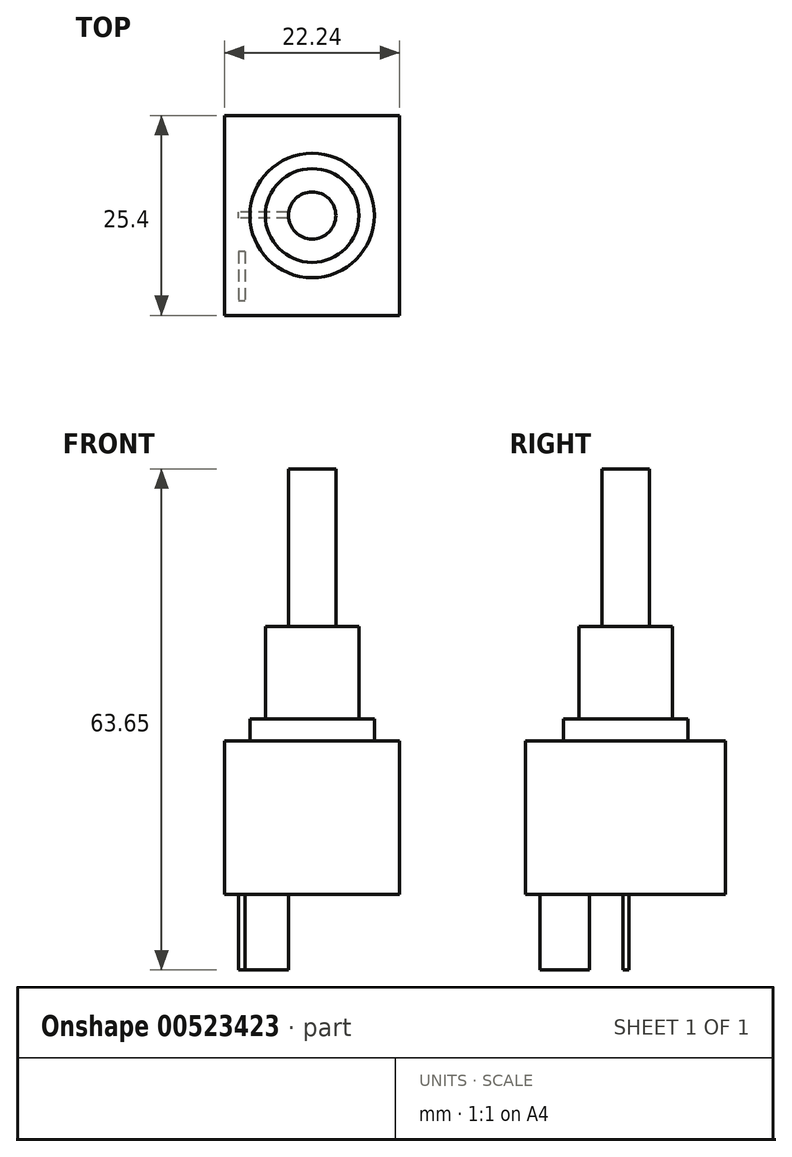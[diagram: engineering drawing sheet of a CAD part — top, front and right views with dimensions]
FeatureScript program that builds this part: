
annotation { "Feature Type Name" : "Feature", "Feature Type Description" : "" }
export const myFeature = defineFeature(function(context is Context, id is Id, definition is map)
    precondition{}
    {
        {
            var Q0;
            Q0=qCreatedBy(makeId("Top.planeOp"),FACE);
            var sketch = newSketch(context, id + "F0", { "sketchPlane" : qUnion([Q0])});
            skLineSegment(sketch, "E0.bottom", {"start": v(11.13, 12.7) * mm, "end": v(-11.12, 12.7) * mm});
            skLineSegment(sketch, "E0.top", {"start": v(11.12, -12.7) * mm, "end": v(-11.13, -12.7) * mm});
            skLineSegment(sketch, "E0.left", {"start": v(11.13, 12.7) * mm, "end": v(11.12, -12.7) * mm});
            skLineSegment(sketch, "E0.right", {"start": v(-11.13, 12.7) * mm, "end": v(-11.13, -12.7) * mm});
            skPoint(sketch, "E0.middle", {"position": v(0, 0) * mm});
            skSolve(sketch);
        }
        {
            var Q0;
            Q0 = qSketchRegion(id + "F0", true);
            extrude(context, id + "F1", {"entities" : qUnion([Q0]), "depth" : 19.5 * mm, "offsetDistance" : 25 * mm});
        }
        {
            var Q0;
            Q0=makeQuery(id+"F1.opExtrude","CAP_FACE",FACE,{"disambiguationData":[OSD([sQuery(id+"F0.wireOp",EDGE,"E0.bottom"),sQuery(id+"F0.wireOp",EDGE,"E0.top"),sQuery(id+"F0.wireOp",EDGE,"E0.left"),sQuery(id+"F0.wireOp",EDGE,"E0.right")])],"isStart":false});
            var sketch = newSketch(context, id + "F2", { "sketchPlane" : qUnion([Q0])});
            skCircle(sketch, "E1", {"center": v(0, 0) * mm, "radius": 7.9 * mm});
            skCircle(sketch, "E2", {"center": v(0, 0) * mm, "radius": 5.95 * mm});
            skSolve(sketch);
        }
        {
            var Q0;
            Q0=makeQuery(id+"F2.imprint","IMPRINT",FACE,{"disambiguationData":[TD([[makeQuery(id+"F2.imprint","IMPRINT",EDGE,{"derivedFrom":sQuery(id+"F2.wireOp",EDGE,"E2")}),1.0]])]});
            var Q1;
            Q1=makeQuery(id+"F2.imprint","IMPRINT",FACE,{"disambiguationData":[TD([[makeQuery(id+"F2.imprint","IMPRINT",EDGE,{"derivedFrom":sQuery(id+"F2.wireOp",EDGE,"E1")}),1.0]])]});
            extrude(context, id + "F3", {"entities" : qUnion([Q0, Q1]), "operationType" : NewBodyOperationType.ADD, "depth" : 2.8 * mm, "offsetDistance" : 25 * mm});
        }
        {
            var Q0;
            Q0=makeQuery(id+"F3.opExtrude","CAP_FACE",FACE,{"disambiguationData":[OSD([sQuery(id+"F2.wireOp",EDGE,"E1")])],"isStart":false});
            var sketch = newSketch(context, id + "F4", { "sketchPlane" : qUnion([Q0])});
            skCircle(sketch, "E3", {"center": v(0, 0) * mm, "radius": 5.95 * mm});
            skSolve(sketch);
        }
        {
            var Q0;
            Q0 = qSketchRegion(id + "F4", true);
            extrude(context, id + "F5", {"entities" : qUnion([Q0]), "operationType" : NewBodyOperationType.ADD, "depth" : 11.75 * mm, "offsetDistance" : 25 * mm});
        }
        {
            var Q0;
            Q0=makeQuery(id+"F5.opExtrude","CAP_FACE",FACE,{"disambiguationData":[OSD([sQuery(id+"F4.wireOp",EDGE,"E3")])],"isStart":false});
            var sketch = newSketch(context, id + "F6", { "sketchPlane" : qUnion([Q0])});
            skCircle(sketch, "E4", {"center": v(0, 0) * mm, "radius": 3 * mm});
            skSolve(sketch);
        }
        {
            var Q0;
            Q0 = qSketchRegion(id + "F6", true);
            extrude(context, id + "F7", {"entities" : qUnion([Q0]), "operationType" : NewBodyOperationType.ADD, "depth" : 20 * mm, "offsetDistance" : 25 * mm});
        }
        {
            var Q0;
            Q0=makeQuery(id+"F1.opExtrude","CAP_FACE",FACE,{"disambiguationData":[OSD([sQuery(id+"F0.wireOp",EDGE,"E0.bottom"),sQuery(id+"F0.wireOp",EDGE,"E0.top"),sQuery(id+"F0.wireOp",EDGE,"E0.left"),sQuery(id+"F0.wireOp",EDGE,"E0.right")])],"isStart":true});
            var sketch = newSketch(context, id + "F8", { "sketchPlane" : qUnion([Q0])});
            skLineSegment(sketch, "E5.bottom", {"start": v(-8.53, 4.6) * mm, "end": v(-9.33, 4.6) * mm});
            skLineSegment(sketch, "E5.top", {"start": v(-8.53, 10.9) * mm, "end": v(-9.33, 10.9) * mm});
            skLineSegment(sketch, "E5.left", {"start": v(-8.53, 4.6) * mm, "end": v(-8.53, 10.9) * mm});
            skLineSegment(sketch, "E5.right", {"start": v(-9.33, 4.6) * mm, "end": v(-9.33, 10.9) * mm});
            skPoint(sketch, "E5.middle", {"position": v(-8.93, 7.75) * mm});
            skLineSegment(sketch, "E6.bottom", {"start": v(-3.03, 0.35) * mm, "end": v(-9.33, 0.35) * mm});
            skLineSegment(sketch, "E6.top", {"start": v(-3.03, -0.45) * mm, "end": v(-9.33, -0.45) * mm});
            skLineSegment(sketch, "E6.left", {"start": v(-3.03, 0.35) * mm, "end": v(-3.03, -0.45) * mm});
            skLineSegment(sketch, "E6.right", {"start": v(-9.33, 0.35) * mm, "end": v(-9.33, -0.45) * mm});
            skPoint(sketch, "E6.middle", {"position": v(-6.18, -0.05) * mm});
            skSolve(sketch);
        }
        {
            var Q0;
            Q0 = qSketchRegion(id + "F8", true);
            extrude(context, id + "F9", {"entities" : qUnion([Q0]), "operationType" : NewBodyOperationType.ADD, "depth" : 9.6 * mm, "offsetDistance" : 25 * mm});
        }
    });
